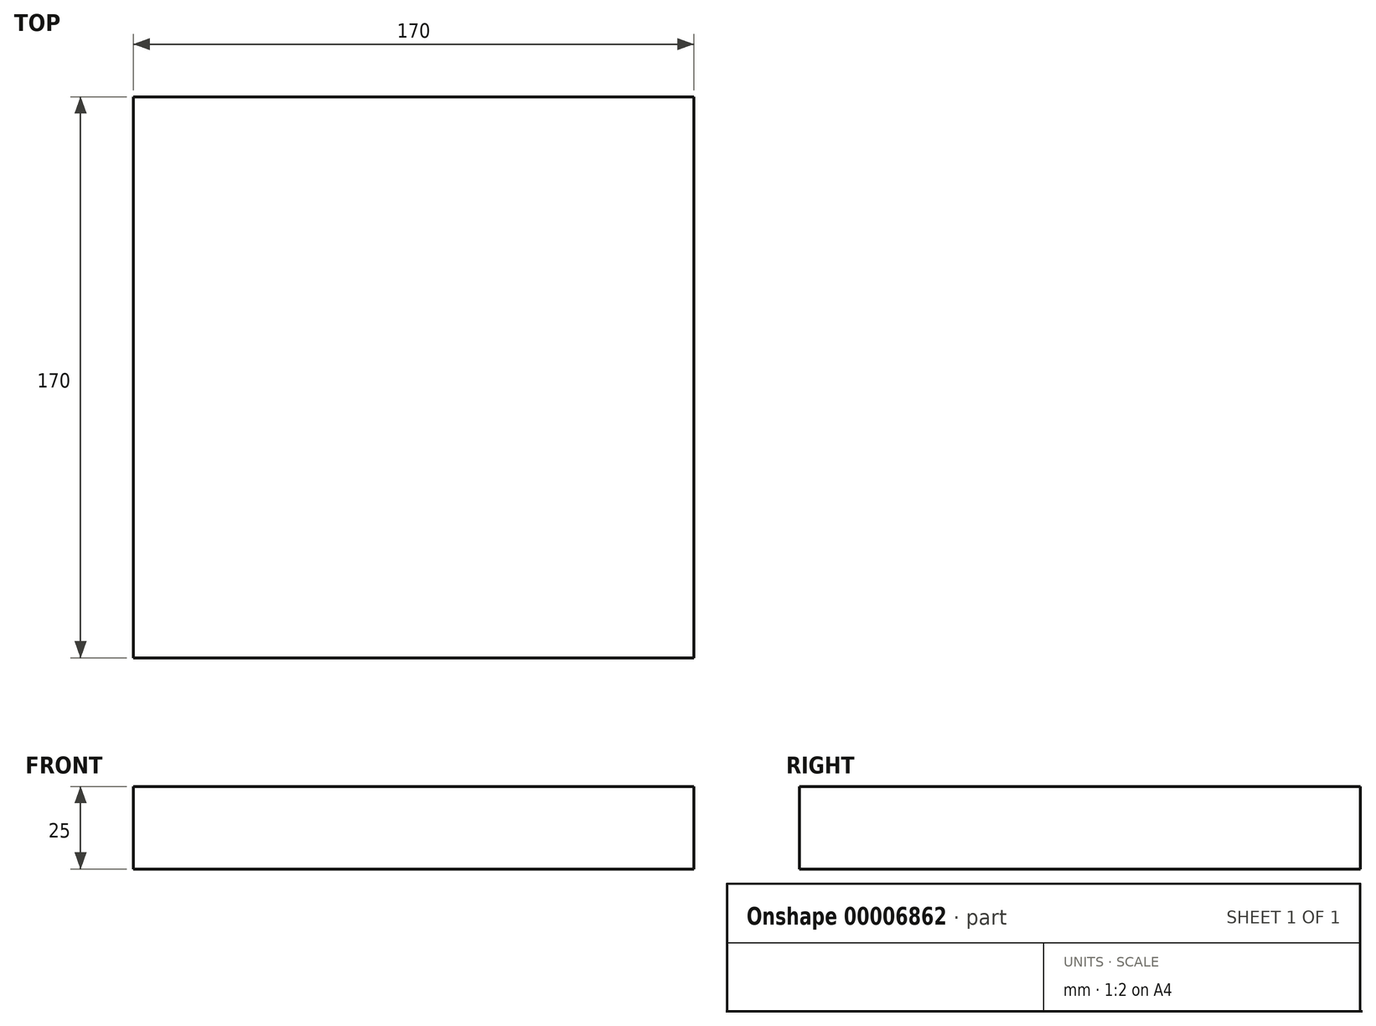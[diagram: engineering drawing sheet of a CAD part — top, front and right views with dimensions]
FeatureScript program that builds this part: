
annotation { "Feature Type Name" : "Feature", "Feature Type Description" : "" }
export const myFeature = defineFeature(function(context is Context, id is Id, definition is map)
    precondition{}
    {
        {
            var Q0;
            Q0=qCreatedBy(makeId("Top.planeOp"),FACE);
            var sketch = newSketch(context, id + "F0", { "sketchPlane" : qUnion([Q0])});
            skLineSegment(sketch, "E0.bottom", {"start": v(-62.35, -80.5) * mm, "end": v(107.65, -80.5) * mm});
            skLineSegment(sketch, "E0.top", {"start": v(-62.35, 89.5) * mm, "end": v(107.65, 89.5) * mm});
            skLineSegment(sketch, "E0.left", {"start": v(-62.35, -80.5) * mm, "end": v(-62.35, 89.5) * mm});
            skLineSegment(sketch, "E0.right", {"start": v(107.65, -80.5) * mm, "end": v(107.65, 89.5) * mm});
            skSolve(sketch);
        }
        {
            var Q0;
            Q0 = qSketchRegion(id + "F0", true);
            extrude(context, id + "F1", {"entities" : qUnion([Q0]), "depth" : 25 * mm});
        }
    });
